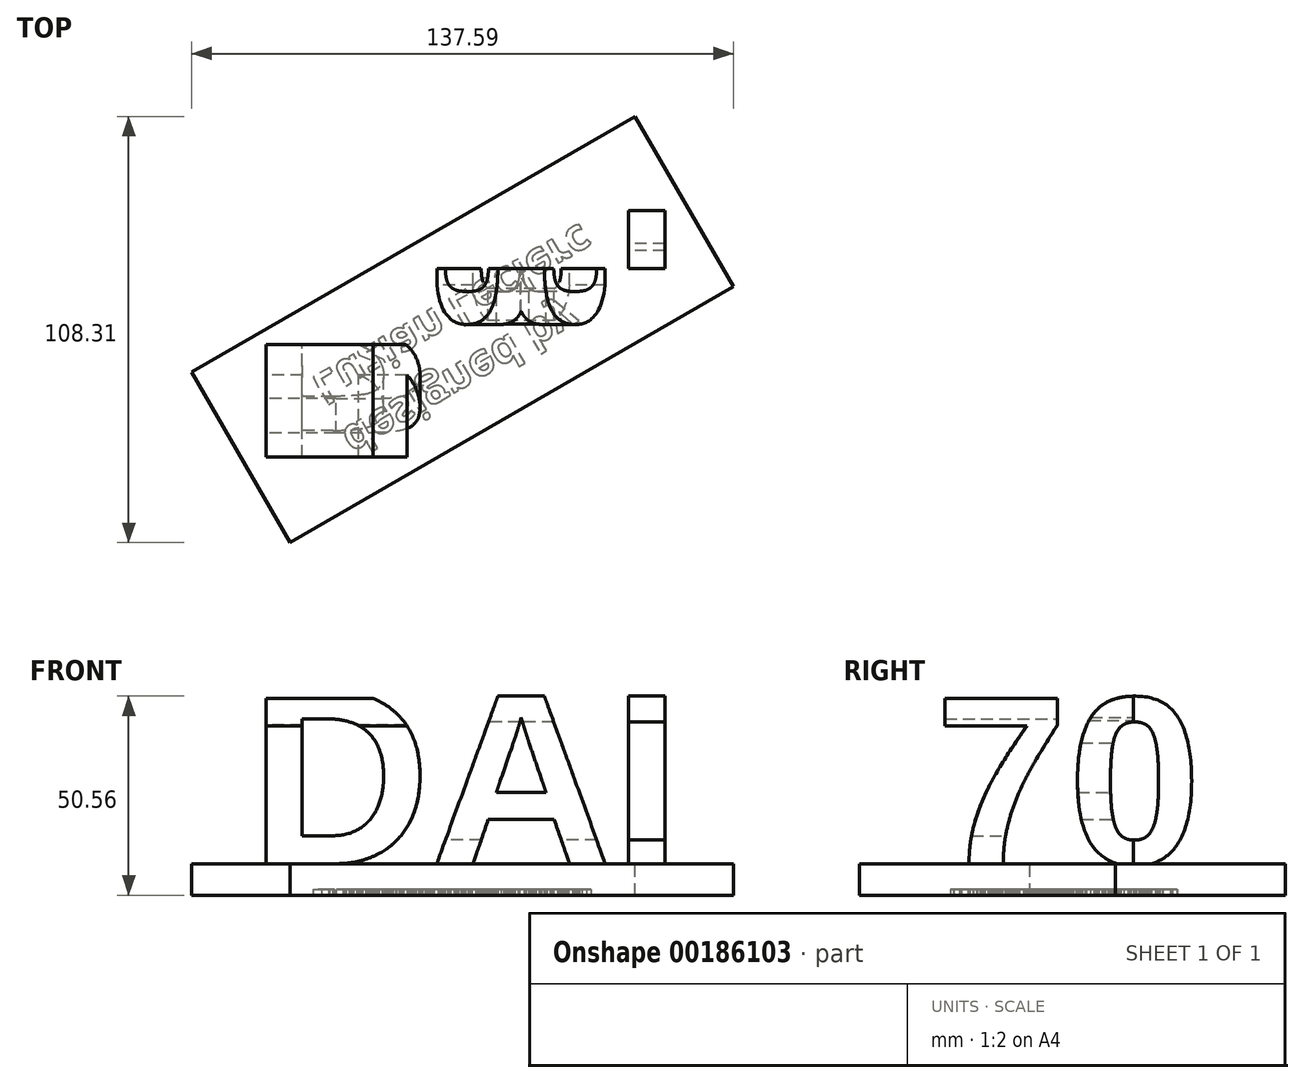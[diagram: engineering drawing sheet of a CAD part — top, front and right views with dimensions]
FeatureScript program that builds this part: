
annotation { "Feature Type Name" : "Feature", "Feature Type Description" : "" }
export const myFeature = defineFeature(function(context is Context, id is Id, definition is map)
    precondition{}
    {
        {
            var Q0;
            Q0=qCreatedBy(makeId("Front.planeOp"),FACE);
            var sketch = newSketch(context, id + "F0", { "sketchPlane" : qUnion([Q0])});
            skPoint(sketch, "E0", {"position": v(55, 22.96) * mm});
            skPoint(sketch, "E1.MirrorP", {"position": v(-55, 22.96) * mm});
            skPoint(sketch, "E2.MirrorP", {"position": v(-55, -22.96) * mm});
            skText(sketch, "E3", { "text": "DAI", "fontName": "Arimo-Bold.ttf"});
            const initialGuessF0  = {"E3": [-0.055, -0.02296, 1, 0, 0.04592]};
            skSetInitialGuess(sketch, initialGuessF0);
            skSolve(sketch);
        }
        {
            var Q0;
            Q0 = qSketchRegion(id + "F0", true);
            extrude(context, id + "F1", {"entities" : qUnion([Q0]), "depth" : (69.51 / 2) * mm, "hasSecondDirection" : true, "secondDirectionOppositeDirection" : true, "secondDirectionDepth" : (69.51 / 2) * mm});
        }
        {
            var Q0;
            Q0=qCreatedBy(makeId("Top.planeOp"),FACE);
            var sketch = newSketch(context, id + "F2", { "sketchPlane" : qUnion([Q0])});
            skLineSegment(sketch, "E4.bottom", {"start": v(-50.73, -34.76) * mm, "end": v(-11.62, -34.76) * mm});
            skLineSegment(sketch, "E4.top", {"start": v(-50.73, -3.26) * mm, "end": v(-11.62, -3.26) * mm});
            skLineSegment(sketch, "E4.left", {"start": v(-50.73, -34.76) * mm, "end": v(-50.73, -3.26) * mm});
            skLineSegment(sketch, "E4.right", {"start": v(-11.62, -34.76) * mm, "end": v(-11.62, -3.26) * mm});
            skLineSegment(sketch, "E5.bottom", {"start": v(-7.35, -3.26) * mm, "end": v(35.44, -3.26) * mm});
            skLineSegment(sketch, "E5.top", {"start": v(-7.35, 15.75) * mm, "end": v(35.44, 15.75) * mm});
            skLineSegment(sketch, "E5.left", {"start": v(-7.35, -3.26) * mm, "end": v(-7.35, 15.75) * mm});
            skLineSegment(sketch, "E5.right", {"start": v(35.44, -3.26) * mm, "end": v(35.44, 15.75) * mm});
            skLineSegment(sketch, "E6.bottom", {"start": v(41.39, 15.75) * mm, "end": v(50.58, 15.75) * mm});
            skLineSegment(sketch, "E6.top", {"start": v(41.39, 34.76) * mm, "end": v(50.58, 34.76) * mm});
            skLineSegment(sketch, "E6.left", {"start": v(41.39, 15.75) * mm, "end": v(41.39, 34.76) * mm});
            skLineSegment(sketch, "E6.right", {"start": v(50.58, 15.75) * mm, "end": v(50.58, 34.76) * mm});
            skSolve(sketch);
        }
        {
            var Q0;
            Q0 = qSketchRegion(id + "F2", true);
            extrude(context, id + "F3", {"entities" : qUnion([Q0]), "operationType" : NewBodyOperationType.INTERSECT, "depth" : 25 * mm, "hasSecondDirection" : true, "secondDirectionOppositeDirection" : true, "secondDirectionDepth" : 25 * mm});
        }
        {
            var Q0;
            Q0=qCreatedBy(makeId("Right.planeOp"),FACE);
            var sketch = newSketch(context, id + "F4", { "sketchPlane" : qUnion([Q0])});
            skText(sketch, "E7", { "text": "70", "fontName": "Arimo-Bold.ttf"});
            skText(sketch, "E8", { "text": "Default text", "fontName": "RobotoSlab-Regular.ttf"});
            const initialGuessF4  = {"E7": [-0.03476, -0.02296, 1, 0, 0.04388], "E8": [-0.04963, 0.03533, 1, 0, 0.02367]};
            skSetInitialGuess(sketch, initialGuessF4);
            skSolve(sketch);
        }
        {
            var Q0;
            Q0 = qSketchRegion(id + "F4", true);
            extrude(context, id + "F5", {"entities" : qUnion([Q0]), "operationType" : NewBodyOperationType.INTERSECT, "depth" : 55 * mm, "hasSecondDirection" : true, "secondDirectionOppositeDirection" : true, "secondDirectionDepth" : 55 * mm});
        }
        {
            var Q0;
            Q0=makeQuery(id+"F1.opExtrude","SWEPT_FACE",FACE,{"disambiguationData":[OSD([sQuery(id+"F0.wireOp",EDGE,"E3.sketch_text.stroke-18")])]});
            var sketch = newSketch(context, id + "F6", { "sketchPlane" : qUnion([Q0])});
            skLineSegment(sketch, "E9", {"start": v(-44.6, 53.9) * mm, "end": v(-69.6, 10.6) * mm});
            skLineSegment(sketch, "E10", {"start": v(-69.6, 10.6) * mm, "end": v(42.99, -54.4) * mm});
            skLineSegment(sketch, "E11", {"start": v(42.99, -54.4) * mm, "end": v(67.99, -11.1) * mm});
            skLineSegment(sketch, "E12", {"start": v(67.99, -11.1) * mm, "end": v(-44.6, 53.9) * mm});
            skSolve(sketch);
        }
        {
            var Q0;
            Q0 = qSketchRegion(id + "F6", true);
            extrude(context, id + "F7", {"entities" : qUnion([Q0]), "operationType" : NewBodyOperationType.ADD, "depth" : 8 * mm});
        }
        {
            var Q0;
            Q0=makeQuery(id+"F7.opExtrude","CAP_FACE",FACE,{"disambiguationData":[OSD([sQuery(id+"F6.wireOp",EDGE,"E9"),sQuery(id+"F6.wireOp",EDGE,"E10"),sQuery(id+"F6.wireOp",EDGE,"E11"),sQuery(id+"F6.wireOp",EDGE,"E12")])],"isStart":false});
            var sketch = newSketch(context, id + "F8", { "sketchPlane" : qUnion([Q0])});
            skText(sketch, "E13", { "text": "designed by\nLuzian Leclerc", "fontName": "OpenSans-Bold.ttf"});
            skLineSegment(sketch, "E14", {"start": v(11.7, 21.4) * mm, "end": v(6.63, 12.63) * mm, "construction": true});
            const initialGuessF8  = {"E13": [-0.03206, 0.0256, 0.86603, -0.5, 0.0081]};
            skSetInitialGuess(sketch, initialGuessF8);
            skSolve(sketch);
        }
        {
            var Q0;
            Q0 = qSketchRegion(id + "F8", true);
            extrude(context, id + "F9", {"entities" : qUnion([Q0]), "operationType" : NewBodyOperationType.REMOVE, "oppositeDirection" : true, "depth" : 1.5 * mm});
        }
    });
